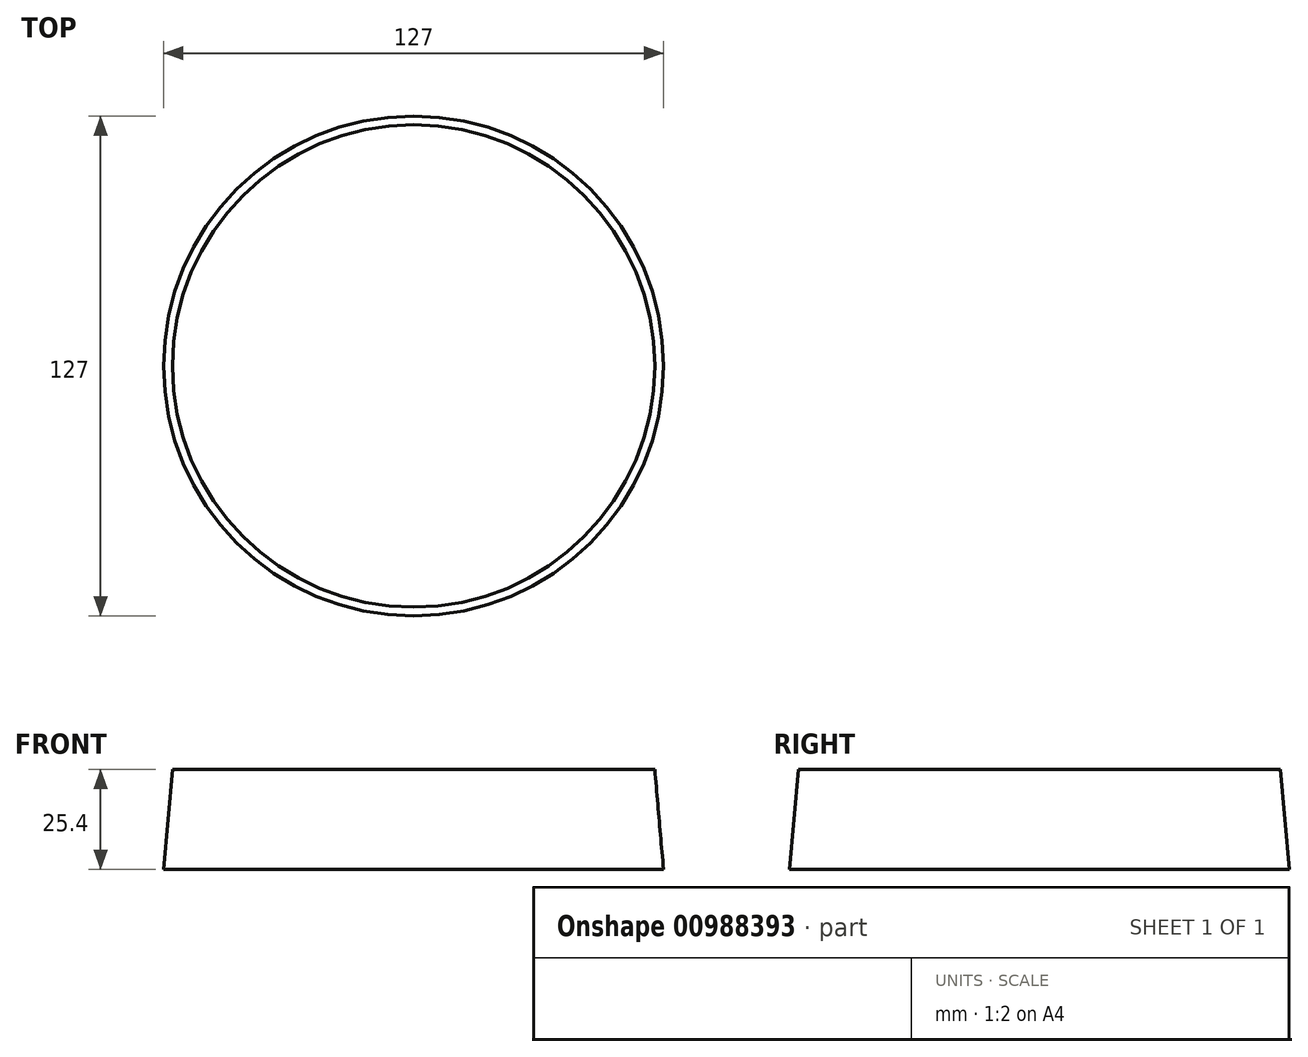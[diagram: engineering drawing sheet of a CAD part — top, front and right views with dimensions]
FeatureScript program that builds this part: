
annotation { "Feature Type Name" : "Feature", "Feature Type Description" : "" }
export const myFeature = defineFeature(function(context is Context, id is Id, definition is map)
    precondition{}
    {
        {
            var Q0;
            Q0=qCreatedBy(makeId("Front.planeOp"),FACE);
            var sketch = newSketch(context, id + "F0", { "sketchPlane" : qUnion([Q0])});
            skLineSegment(sketch, "E0", {"start": v(0, 0) * mm, "end": v(63.5, 0) * mm});
            skLineSegment(sketch, "E1", {"start": v(63.5, 0) * mm, "end": v(61.28, 25.4) * mm});
            skLineSegment(sketch, "E2", {"start": v(61.28, 25.4) * mm, "end": v(0, 25.4) * mm});
            skLineSegment(sketch, "E3", {"start": v(0, 25.4) * mm, "end": v(0, 0) * mm});
            skLineSegment(sketch, "E4", {"start": v(61.28, 25.4) * mm, "end": v(61.28, 0) * mm, "construction": true});
            skSolve(sketch);
        }
        {
            var Q0;
            Q0=makeQuery(id+"F0.imprint","IMPRINT",FACE,{"disambiguationData":[TD([[makeQuery(id+"F0.imprint","IMPRINT",EDGE,{"derivedFrom":sQuery(id+"F0.wireOp",EDGE,"E0")}),1.0]])]});
            var Q1;
            Q1=sQuery(id+"F0.wireOp",EDGE,"E3");
            revolve(context, id + "F1", {"surfaceOperationType" : NewSurfaceOperationType.NEW, "entities" : qUnion([Q0]), "axis" : qUnion([Q1]), "revolveType" : RevolveType.FULL});
        }
    });
